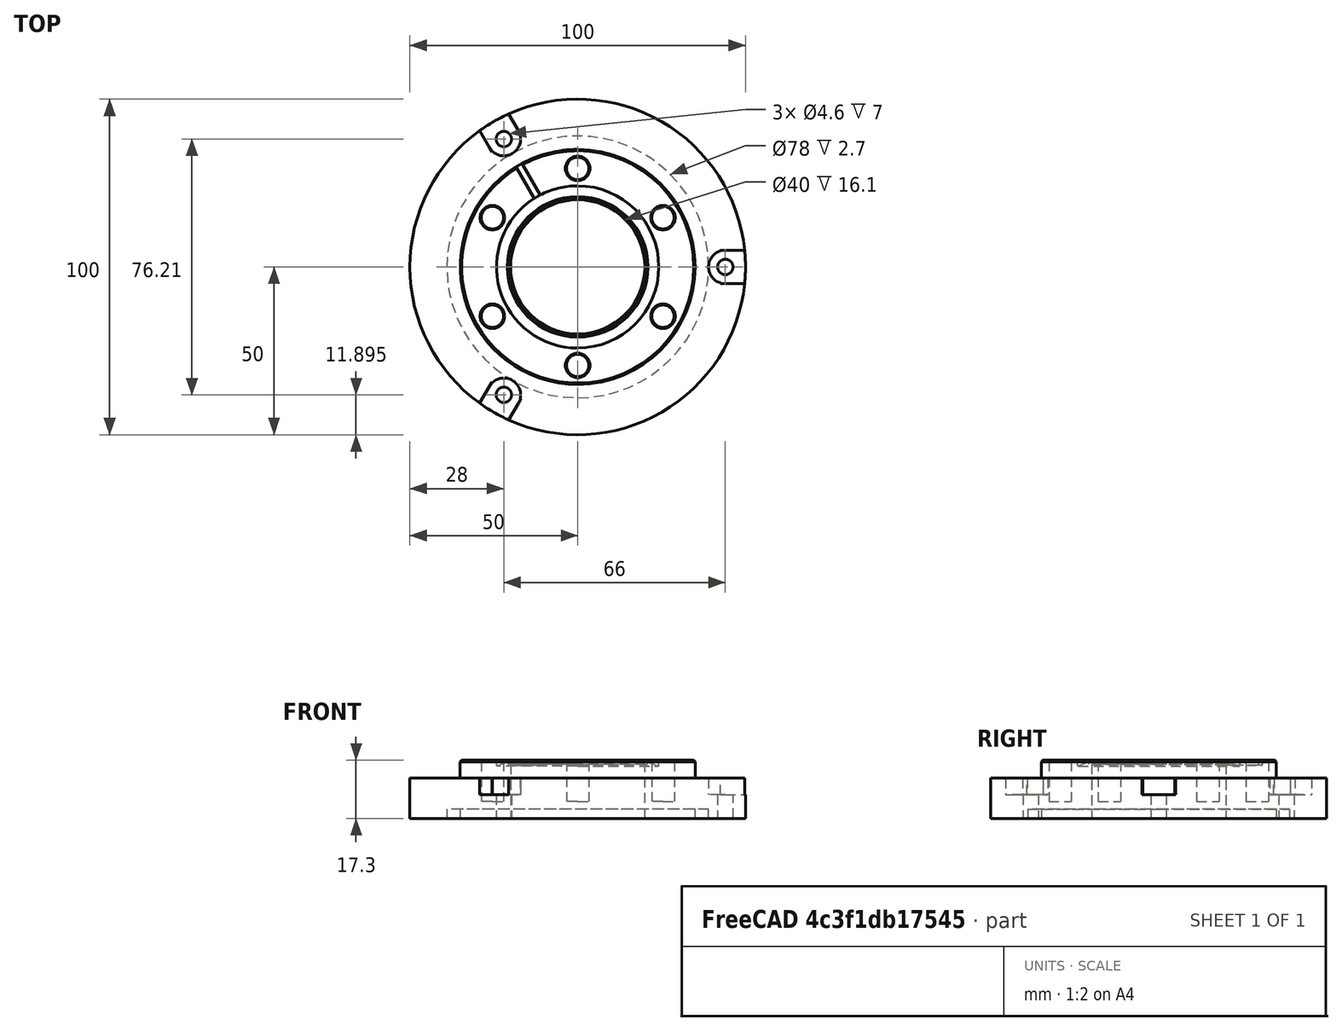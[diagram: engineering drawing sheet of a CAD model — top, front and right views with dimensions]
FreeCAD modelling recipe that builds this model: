
FCSTD DOCUMENT  (FreeCAD 0.20R29603 (Git))
Label: PhilippsXL30_FlangeToCF35_CF40_ZeroLengthAdapter_100
License: All rights reserved
LicenseURL: http://en.wikipedia.org/wiki/All_rights_reserved
objects: TechDraw::DrawViewDimension×26, Part::Cylinder×5, TechDraw::DrawProjGroupItem×4, Part::Compound×3, Part::Cut×3, TechDraw::DrawSVGTemplate×2, TechDraw::DrawProjGroup×2, TechDraw::DrawPage×2, Part::Feature×1, App::Link×1, Part::MultiFuse×1, TechDraw::DrawViewSection×1
note: 13 computed .brp shape members not serialized (recipe doc carries the construction recipe); baked Part::Feature solids carry a one-line shape summary decoded from their .brp
EXTERNAL_REF file=PhilippsXL30_Blindflange_100.FCStd obj=Cut001_solid001

FEATURE [Part::Feature] Solid  label="CF35 Flange"
  Placement = pos=(0,0,4.6) rot=(1,0,0;1.5708rad)
  shape: bbox 70 x 70 x 12.7 mm, 58 faces (baked)
FEATURE [Part::Cylinder] Cylinder004  label="Zylinder004"
  Angle = 360
  AttacherType = Attacher::AttachEngine3D
  FirstAngle = 0
  Height = 12
  Placement = pos=(42.5,0,7) rot=(0,0,1;0rad)
  Radius = 5
  SecondAngle = 0
FEATURE [Part::Cylinder] Cylinder005  label="Zylinder005"
  Angle = 360
  AttacherType = Attacher::AttachEngine3D
  FirstAngle = 0
  Height = 12
  Placement = pos=(42.5,0,7) rot=(0,0,1;0rad)
  Radius = 5
  SecondAngle = 0
FEATURE [Part::Compound] Compound
  Links = -> [Cylinder005]
  Placement = pos=(0,0,0) rot=(0,0,1;2.0944rad)
FEATURE [Part::Cylinder] Cylinder006  label="Zylinder006"
  Angle = 360
  AttacherType = Attacher::AttachEngine3D
  FirstAngle = 0
  Height = 12
  Placement = pos=(42.5,0,7) rot=(0,0,1;0rad)
  Radius = 5
  SecondAngle = 0
FEATURE [Part::Compound] Compound001
  Links = -> [Cylinder006]
  Placement = pos=(0,0,0) rot=(0,0,1;4.18879rad)
FEATURE [Part::Compound] Compound002
  Links = -> [Compound001,Cylinder004,Compound]
FEATURE [Part::Cut] Cut
  Base = -> Solid
  Tool = -> Compound002
FEATURE [Part::Cylinder] Cylinder  label="Zylinder"
  Angle = 360
  AttacherType = Attacher::AttachEngine3D
  FirstAngle = 0
  Height = 50
  Placement = pos=(0,0,-1) rot=(0,0,1;0rad)
  Radius = 20
  SecondAngle = 0
FEATURE [App::Link] Link001  label="Cut001 (Solid)001"
  LinkedObject = -> <external PhilippsXL30_Blindflange_100.FCStd>#Cut001_solid001
FEATURE [Part::Cylinder] Cylinder008  label="Zylinder008"
  Angle = 360
  AttacherType = Attacher::AttachEngine3D
  FirstAngle = 0
  Height = 12.5
  Placement = pos=(0,0,5) rot=(0,0,1;0rad)
  Radius = 34.95
  SecondAngle = 0
FEATURE [Part::Cut] Cut003
  Base = -> Link001
  Tool = -> Cylinder008
FEATURE [Part::MultiFuse] Fusion
  Shapes = -> [Cut,Cut003]
FEATURE [Part::Cut] Cut002
  Base = -> Fusion
  Tool = -> Cylinder
FEATURE [TechDraw::DrawSVGTemplate] Template
  EditableTexts = Designed_by_Name=Thomas Spielauer; FC-Date=2023-07-05; FC-SC=mm; FC-SH=01; FC-Title=Philips XL30 CF40 Adapter; Subtitle=100mm flange variant
  Height = 210
  Orientation = 1
  Width = 297
FEATURE [TechDraw::DrawProjGroupItem] ProjItem  label="Front"
  CoarseView = false
  Direction = (0,0,1)
  Focus = 100
  HardHidden = false
  IsoCount = 0
  IsoHidden = false
  IsoVisible = false
  LockPosition = true
  Perspective = false
  Rotation = 0
  RotationVector = (0,1,0)
  ScaleType = 2
  SeamHidden = false
  SeamVisible = true
  SmoothHidden = false
  SmoothVisible = true
  Source = -> [Cut002]
  Type = 0
  X = 0
  XDirection = (0,1,0)
  Y = 0
FEATURE [TechDraw::DrawProjGroupItem] ProjItem003  label="Top"
  CoarseView = false
  Direction = (-1,0,0)
  Focus = 100
  HardHidden = false
  IsoCount = 0
  IsoHidden = false
  IsoVisible = false
  LockPosition = false
  Perspective = false
  Rotation = 0
  RotationVector = (1,0,0)
  ScaleType = 2
  SeamHidden = false
  SeamVisible = true
  SmoothHidden = false
  SmoothVisible = true
  Source = -> [Cut002]
  Type = 4
  X = 0
  XDirection = (0,1,0)
  Y = -115
FEATURE [TechDraw::DrawViewDimension] Dimension007
  AngleOverride = false
  Arbitrary = false
  ArbitraryTolerances = false
  EqualTolerance = true
  ExtensionAngle = 0
  FormatSpec = R%.2w
  FormatSpecOverTolerance = %+.2w
  FormatSpecUnderTolerance = %+.2w
  Inverted = false
  LineAngle = 0
  LockPosition = false
  MeasureType = 1
  OverTolerance = 0
  References2D = -> [ProjItem]
  Rotation = 0
  ScaleType = 0
  TheoreticalExact = false
  Type = 4
  UnderTolerance = 0
  X = -1.26969
  Y = 60.8859
FEATURE [TechDraw::DrawViewDimension] Dimension012
  AngleOverride = false
  Arbitrary = false
  ArbitraryTolerances = false
  EqualTolerance = true
  ExtensionAngle = 0
  FormatSpec = ⌀%.2w
  FormatSpecOverTolerance = %+.2w
  FormatSpecUnderTolerance = %+.2w
  Inverted = false
  LineAngle = 0
  LockPosition = false
  MeasureType = 1
  OverTolerance = 0
  References2D = -> [ProjItem]
  Rotation = 0
  ScaleType = 0
  TheoreticalExact = false
  Type = 5
  UnderTolerance = 0
  X = 40.6138
  Y = 54.0598
FEATURE [TechDraw::DrawViewDimension] Dimension015
  AngleOverride = false
  Arbitrary = false
  ArbitraryTolerances = false
  EqualTolerance = true
  ExtensionAngle = 0
  FormatSpec = %.2w
  FormatSpecOverTolerance = %+.2w
  FormatSpecUnderTolerance = %+.2w
  Inverted = false
  LineAngle = 0
  LockPosition = false
  MeasureType = 1
  OverTolerance = 0
  References2D = -> [ProjItem]
  Rotation = 0
  ScaleType = 0
  TheoreticalExact = false
  Type = 0
  UnderTolerance = 0
  X = 58.2576
  Y = 40.308
FEATURE [TechDraw::DrawViewDimension] Dimension016
  AngleOverride = false
  Arbitrary = false
  ArbitraryTolerances = false
  EqualTolerance = true
  ExtensionAngle = 0
  FormatSpec = ⌀%.2w
  FormatSpecOverTolerance = %+.2w
  FormatSpecUnderTolerance = %+.2w
  Inverted = false
  LineAngle = 0
  LockPosition = false
  MeasureType = 1
  OverTolerance = 0
  References2D = -> [ProjItem]
  Rotation = 0
  ScaleType = 0
  TheoreticalExact = false
  Type = 5
  UnderTolerance = 0
  X = -52.3492
  Y = 45.3065
FEATURE [TechDraw::DrawViewDimension] Dimension017
  AngleOverride = false
  Arbitrary = false
  ArbitraryTolerances = false
  EqualTolerance = true
  ExtensionAngle = 0
  FormatSpec = ⌀%.2w (6x M6)
  FormatSpecOverTolerance = %+.2w
  FormatSpecUnderTolerance = %+.2w
  Inverted = false
  LineAngle = 0
  LockPosition = false
  MeasureType = 1
  OverTolerance = 0
  References2D = -> [ProjItem]
  Rotation = 0
  ScaleType = 0
  TheoreticalExact = false
  Type = 5
  UnderTolerance = 0
  X = -40.9728
  Y = 56.0349
FEATURE [TechDraw::DrawViewDimension] Dimension018
  AngleOverride = false
  Arbitrary = false
  ArbitraryTolerances = false
  EqualTolerance = true
  ExtensionAngle = 0
  FormatSpec = %.2w
  FormatSpecOverTolerance = %+.2w
  FormatSpecUnderTolerance = %+.2w
  Inverted = false
  LineAngle = 0
  LockPosition = false
  MeasureType = 1
  OverTolerance = 0
  References2D = -> [ProjItem003]
  Rotation = 0
  ScaleType = 0
  TheoreticalExact = false
  Type = 0
  UnderTolerance = 0
  X = -0.313919
  Y = -18.7458
FEATURE [TechDraw::DrawViewDimension] Dimension019
  AngleOverride = false
  Arbitrary = false
  ArbitraryTolerances = false
  EqualTolerance = true
  ExtensionAngle = 0
  FormatSpec = %.2w
  FormatSpecOverTolerance = %+.2w
  FormatSpecUnderTolerance = %+.2w
  Inverted = false
  LineAngle = 0
  LockPosition = false
  MeasureType = 1
  OverTolerance = 0
  References2D = -> [ProjItem003]
  Rotation = 0
  ScaleType = 0
  TheoreticalExact = false
  Type = 0
  UnderTolerance = 0
  X = 52.4225
  Y = -14.6035
FEATURE [TechDraw::DrawSVGTemplate] Template001
  EditableTexts = Designed_by_Name=Thomas Spielauer; FC-Date=2023-07-05; FC-SC=mm; FC-SH=02; FC-Title=Philips XL30 CF40 Adapter; Subtitle=100mm flange variant
  Height = 210
  Orientation = 1
  Width = 297
FEATURE [TechDraw::DrawProjGroupItem] ProjItem004  label="Front001"
  CoarseView = false
  Direction = (0,0,1)
  Focus = 100
  HardHidden = false
  IsoCount = 0
  IsoHidden = false
  IsoVisible = false
  LockPosition = true
  Perspective = false
  Rotation = 0
  RotationVector = (0,1,0)
  ScaleType = 2
  SeamHidden = false
  SeamVisible = true
  SmoothHidden = false
  SmoothVisible = true
  Source = -> [Cut002]
  Type = 0
  X = 0
  XDirection = (0,1,0)
  Y = 0
FEATURE [TechDraw::DrawProjGroup] ProjGroup001
  Anchor = -> ProjItem004
  AutoDistribute = true
  LockPosition = false
  ProjectionType = 0
  Rotation = 0
  ScaleType = 0
  Source = -> [Cut002]
  Views = -> [ProjItem004]
  X = 80.4015
  Y = 138.514
  spacingX = 15
  spacingY = 15
FEATURE [TechDraw::DrawViewSection] SectionView  label="Section  - "
  BaseView = -> ProjItem004
  CoarseView = false
  CutSurfaceDisplay = 2
  Direction = (0,-1,0)
  FileGeomPattern = <path>
  FileHatchPattern = <path>
  Focus = 100
  FuseBeforeCut = false
  HardHidden = false
  HatchScale = 1
  IsoCount = 0
  IsoHidden = false
  IsoVisible = false
  LockPosition = false
  NameGeomPattern = Diamond
  Perspective = false
  Rotation = 0
  ScaleType = 2
  SeamHidden = false
  SeamVisible = true
  SectionDirection = 0
  SectionNormal = (0,-1,0)
  SectionOrigin = (0,0,8.65)
  SmoothHidden = false
  SmoothVisible = true
  Source = -> [Cut002]
  X = 193.115
  XDirection = (0,0,1)
  Y = 128.608
FEATURE [TechDraw::DrawViewDimension] Dimension020
  AngleOverride = false
  Arbitrary = false
  ArbitraryTolerances = false
  EqualTolerance = true
  ExtensionAngle = 0
  FormatSpec = %.2w
  FormatSpecOverTolerance = %+.2w
  FormatSpecUnderTolerance = %+.2w
  Inverted = false
  LineAngle = 0
  LockPosition = false
  MeasureType = 1
  OverTolerance = 0
  References2D = -> [SectionView]
  Rotation = 0
  ScaleType = 0
  TheoreticalExact = false
  Type = 0
  UnderTolerance = 0
  X = -3.19245
  Y = 66.0613
FEATURE [TechDraw::DrawViewDimension] Dimension021
  AngleOverride = false
  Arbitrary = false
  ArbitraryTolerances = false
  EqualTolerance = true
  ExtensionAngle = 0
  FormatSpec = %.2w
  FormatSpecOverTolerance = %+.2w
  FormatSpecUnderTolerance = %+.2w
  Inverted = false
  LineAngle = 0
  LockPosition = false
  MeasureType = 1
  OverTolerance = 0
  References2D = -> [SectionView]
  Rotation = 0
  ScaleType = 0
  TheoreticalExact = false
  Type = 0
  UnderTolerance = 0
  X = 14.208
  Y = 60.5542
FEATURE [TechDraw::DrawViewDimension] Dimension022
  AngleOverride = false
  Arbitrary = false
  ArbitraryTolerances = false
  EqualTolerance = true
  ExtensionAngle = 0
  FormatSpec = %.2w
  FormatSpecOverTolerance = %+.2w
  FormatSpecUnderTolerance = %+.2w
  Inverted = false
  LineAngle = 0
  LockPosition = false
  MeasureType = 1
  OverTolerance = 0
  References2D = -> [SectionView]
  Rotation = 0
  ScaleType = 0
  TheoreticalExact = false
  Type = 0
  UnderTolerance = 0
  X = -20.8291
  Y = 47.7164
FEATURE [TechDraw::DrawViewDimension] Dimension023
  AngleOverride = false
  Arbitrary = false
  ArbitraryTolerances = false
  EqualTolerance = true
  ExtensionAngle = 0
  FormatSpec = %.2w
  FormatSpecOverTolerance = %+.2w
  FormatSpecUnderTolerance = %+.2w
  Inverted = false
  LineAngle = 0
  LockPosition = false
  MeasureType = 1
  OverTolerance = 0
  References2D = -> [SectionView]
  Rotation = 0
  ScaleType = 0
  TheoreticalExact = false
  Type = 0
  UnderTolerance = 0
  X = -36.0172
  Y = 38.6403
FEATURE [TechDraw::DrawViewDimension] Dimension024
  AngleOverride = false
  Arbitrary = false
  ArbitraryTolerances = false
  EqualTolerance = true
  ExtensionAngle = 0
  FormatSpec = %.2w
  FormatSpecOverTolerance = %+.2w
  FormatSpecUnderTolerance = %+.2w
  Inverted = false
  LineAngle = 0
  LockPosition = false
  MeasureType = 1
  OverTolerance = 0
  References2D = -> [SectionView]
  Rotation = 0
  ScaleType = 0
  TheoreticalExact = false
  Type = 0
  UnderTolerance = 0
  X = -21.915
  Y = 18.1567
FEATURE [TechDraw::DrawViewDimension] Dimension025
  AngleOverride = false
  Arbitrary = false
  ArbitraryTolerances = false
  EqualTolerance = true
  ExtensionAngle = 0
  FormatSpec = %.2w
  FormatSpecOverTolerance = %+.2w
  FormatSpecUnderTolerance = %+.2w
  Inverted = false
  LineAngle = 0
  LockPosition = false
  MeasureType = 1
  OverTolerance = 0
  References2D = -> [SectionView]
  Rotation = 0
  ScaleType = 0
  TheoreticalExact = false
  Type = 0
  UnderTolerance = 0
  X = -13.979
  Y = -60.471
FEATURE [TechDraw::DrawViewDimension] Dimension026
  AngleOverride = false
  Arbitrary = false
  ArbitraryTolerances = false
  EqualTolerance = true
  ExtensionAngle = 0
  FormatSpec = %.2w
  FormatSpecOverTolerance = %+.2w
  FormatSpecUnderTolerance = %+.2w
  Inverted = false
  LineAngle = 0
  LockPosition = false
  MeasureType = 1
  OverTolerance = 0
  References2D = -> [SectionView]
  Rotation = 0
  ScaleType = 0
  TheoreticalExact = false
  Type = 0
  UnderTolerance = 0
  X = 14.3909
  Y = -57.6165
FEATURE [TechDraw::DrawViewDimension] Dimension027
  AngleOverride = false
  Arbitrary = false
  ArbitraryTolerances = false
  EqualTolerance = true
  ExtensionAngle = 0
  FormatSpec = %.2w (CF40 knife edge)
  FormatSpecOverTolerance = %+.2w
  FormatSpecUnderTolerance = %+.2w
  Inverted = false
  LineAngle = 0
  LockPosition = false
  MeasureType = 1
  OverTolerance = 0
  References2D = -> [SectionView]
  Rotation = 0
  ScaleType = 0
  TheoreticalExact = false
  Type = 0
  UnderTolerance = 0
  X = 51.4939
  Y = 1.25347
FEATURE [TechDraw::DrawViewDimension] Dimension028
  AngleOverride = false
  Arbitrary = false
  ArbitraryTolerances = false
  EqualTolerance = true
  ExtensionAngle = 0
  FormatSpec = %.2w
  FormatSpecOverTolerance = %+.2w
  FormatSpecUnderTolerance = %+.2w
  Inverted = false
  LineAngle = 0
  LockPosition = false
  MeasureType = 1
  OverTolerance = 0
  References2D = -> [SectionView]
  Rotation = 0
  ScaleType = 0
  TheoreticalExact = false
  Type = 0
  UnderTolerance = 0
  X = 35.1516
  Y = 5.12687
FEATURE [TechDraw::DrawPage] Page001
  KeepUpdated = true
  NextBalloonIndex = 1
  ProjectionType = 0
  Template = -> Template001
  Views = -> [ProjGroup001,SectionView,Dimension020,Dimension021,Dimension022,Dimension023,Dimension024,Dimension025,Dimension026,Dimension027,Dimension028]
FEATURE [TechDraw::DrawViewDimension] Dimension031
  AngleOverride = false
  Arbitrary = false
  ArbitraryTolerances = false
  EqualTolerance = true
  ExtensionAngle = 0
  FormatSpec = R%.2w
  FormatSpecOverTolerance = %+.2w
  FormatSpecUnderTolerance = %+.2w
  Inverted = false
  LineAngle = 0
  LockPosition = false
  MeasureType = 1
  OverTolerance = 0
  References2D = -> [ProjItem]
  Rotation = 0
  ScaleType = 0
  TheoreticalExact = false
  Type = 4
  UnderTolerance = 0
  X = -57.2589
  Y = -22.9275
FEATURE [TechDraw::DrawViewDimension] Dimension
  AngleOverride = false
  Arbitrary = false
  ArbitraryTolerances = false
  EqualTolerance = true
  ExtensionAngle = 0
  FormatSpec = %.2w
  FormatSpecOverTolerance = %+.2w
  FormatSpecUnderTolerance = %+.2w
  Inverted = false
  LineAngle = 0
  LockPosition = false
  MeasureType = 1
  OverTolerance = 0
  References2D = -> [ProjItem003]
  Rotation = 0
  ScaleType = 0
  TheoreticalExact = false
  Type = 0
  UnderTolerance = 0
  X = -0.678066
  Y = 30.3595
FEATURE [TechDraw::DrawViewDimension] Dimension032
  AngleOverride = false
  Arbitrary = false
  ArbitraryTolerances = false
  EqualTolerance = true
  ExtensionAngle = 0
  FormatSpec = %.2w
  FormatSpecOverTolerance = %+.2w
  FormatSpecUnderTolerance = %+.2w
  Inverted = false
  LineAngle = 0
  LockPosition = false
  MeasureType = 1
  OverTolerance = 0
  References2D = -> [ProjItem003]
  Rotation = 0
  ScaleType = 0
  TheoreticalExact = false
  Type = 0
  UnderTolerance = 0
  X = -61.7531
  Y = 5.37362
FEATURE [TechDraw::DrawProjGroupItem] ProjItem001  label="Rear"
  CoarseView = false
  Direction = (0,0,-1)
  Focus = 100
  HardHidden = false
  IsoCount = 0
  IsoHidden = false
  IsoVisible = false
  LockPosition = false
  Perspective = false
  Rotation = 0
  RotationVector = (1,0,0)
  ScaleType = 2
  SeamHidden = false
  SeamVisible = true
  SmoothHidden = false
  SmoothVisible = true
  Source = -> [Cut002]
  Type = 3
  X = 115
  XDirection = (0,-1,0)
  Y = 0
FEATURE [TechDraw::DrawProjGroup] ProjGroup
  Anchor = -> ProjItem
  AutoDistribute = true
  LockPosition = false
  ProjectionType = 0
  Rotation = 0
  ScaleType = 0
  Source = -> [Cut002]
  Views = -> [ProjItem,ProjItem001,ProjItem003]
  X = 76.1231
  Y = 135.662
  spacingX = 15
  spacingY = 15
FEATURE [TechDraw::DrawViewDimension] Dimension003
  AngleOverride = false
  Arbitrary = false
  ArbitraryTolerances = false
  EqualTolerance = true
  ExtensionAngle = 0
  FormatSpec = ⌀%.2w
  FormatSpecOverTolerance = %+.2w
  FormatSpecUnderTolerance = %+.2w
  Inverted = false
  LineAngle = 0
  LockPosition = false
  MeasureType = 1
  OverTolerance = 0
  References2D = -> [ProjItem001]
  Rotation = 0
  ScaleType = 0
  TheoreticalExact = false
  Type = 5
  UnderTolerance = 0
  X = 37.3868
  Y = 50.5334
FEATURE [TechDraw::DrawViewDimension] Dimension004
  AngleOverride = false
  Arbitrary = false
  ArbitraryTolerances = false
  EqualTolerance = true
  ExtensionAngle = 0
  FormatSpec = ⌀%.2w
  FormatSpecOverTolerance = %+.2w
  FormatSpecUnderTolerance = %+.2w
  Inverted = false
  LineAngle = 0
  LockPosition = false
  MeasureType = 1
  OverTolerance = 0
  References2D = -> [ProjItem001]
  Rotation = 0
  ScaleType = 0
  TheoreticalExact = false
  Type = 5
  UnderTolerance = 0
  X = 44.0719
  Y = 46.338
FEATURE [TechDraw::DrawViewDimension] Dimension005
  AngleOverride = false
  Arbitrary = false
  ArbitraryTolerances = false
  EqualTolerance = true
  ExtensionAngle = 0
  FormatSpec = ⌀%.2w
  FormatSpecOverTolerance = %+.2w
  FormatSpecUnderTolerance = %+.2w
  Inverted = false
  LineAngle = 0
  LockPosition = false
  MeasureType = 1
  OverTolerance = 0
  References2D = -> [ProjItem001]
  Rotation = 0
  ScaleType = 0
  TheoreticalExact = false
  Type = 5
  UnderTolerance = 0
  X = 48.9256
  Y = 41.6983
FEATURE [TechDraw::DrawViewDimension] Dimension008
  AngleOverride = false
  Arbitrary = false
  ArbitraryTolerances = false
  EqualTolerance = true
  ExtensionAngle = 0
  FormatSpec = %.2w
  FormatSpecOverTolerance = %+.2w
  FormatSpecUnderTolerance = %+.2w
  Inverted = false
  LineAngle = 0
  LockPosition = false
  MeasureType = 1
  OverTolerance = 0
  References2D = -> [ProjItem001]
  Rotation = 0
  ScaleType = 0
  TheoreticalExact = false
  Type = 6
  UnderTolerance = 0
  X = 57.7233
  Y = -33.2236
FEATURE [TechDraw::DrawViewDimension] Dimension010
  AngleOverride = false
  Arbitrary = false
  ArbitraryTolerances = false
  EqualTolerance = true
  ExtensionAngle = 0
  FormatSpec = ⌀%.2w (3x)
  FormatSpecOverTolerance = %+.2w
  FormatSpecUnderTolerance = %+.2w
  Inverted = false
  LineAngle = 0
  LockPosition = false
  MeasureType = 1
  OverTolerance = 0
  References2D = -> [ProjItem001]
  Rotation = 0
  ScaleType = 0
  TheoreticalExact = false
  Type = 5
  UnderTolerance = 0
  X = -39.5129
  Y = 51.575
FEATURE [TechDraw::DrawViewDimension] Dimension011
  AngleOverride = false
  Arbitrary = false
  ArbitraryTolerances = false
  EqualTolerance = true
  ExtensionAngle = 0
  FormatSpec = ⌀%.2w
  FormatSpecOverTolerance = %+.2w
  FormatSpecUnderTolerance = %+.2w
  Inverted = false
  LineAngle = 0
  LockPosition = false
  MeasureType = 1
  OverTolerance = 0
  References2D = -> [ProjItem001]
  Rotation = 0
  ScaleType = 0
  TheoreticalExact = false
  Type = 5
  UnderTolerance = 0
  X = -20.9799
  Y = -22.9677
FEATURE [TechDraw::DrawViewDimension] Dimension033
  AngleOverride = false
  Arbitrary = false
  ArbitraryTolerances = false
  EqualTolerance = true
  ExtensionAngle = 0
  FormatSpec = R%.2w
  FormatSpecOverTolerance = %+.2w
  FormatSpecUnderTolerance = %+.2w
  Inverted = false
  LineAngle = 0
  LockPosition = false
  MeasureType = 1
  OverTolerance = 0
  References2D = -> [ProjItem001]
  Rotation = 0
  ScaleType = 0
  TheoreticalExact = false
  Type = 4
  UnderTolerance = 0
  X = 19.2921
  Y = -12.3401
FEATURE [TechDraw::DrawPage] Page
  KeepUpdated = true
  NextBalloonIndex = 1
  ProjectionType = 0
  Template = -> Template
  Views = -> [ProjGroup,Dimension003,Dimension004,Dimension005,Dimension007,Dimension008,Dimension010,Dimension011,Dimension012,Dimension015,Dimension016,Dimension017,Dimension018,Dimension019,Dimension031,Dimension,Dimension032,Dimension033]
note: 2 file-system paths scrubbed to <path> (originals preserved in the JSON sidecar)
